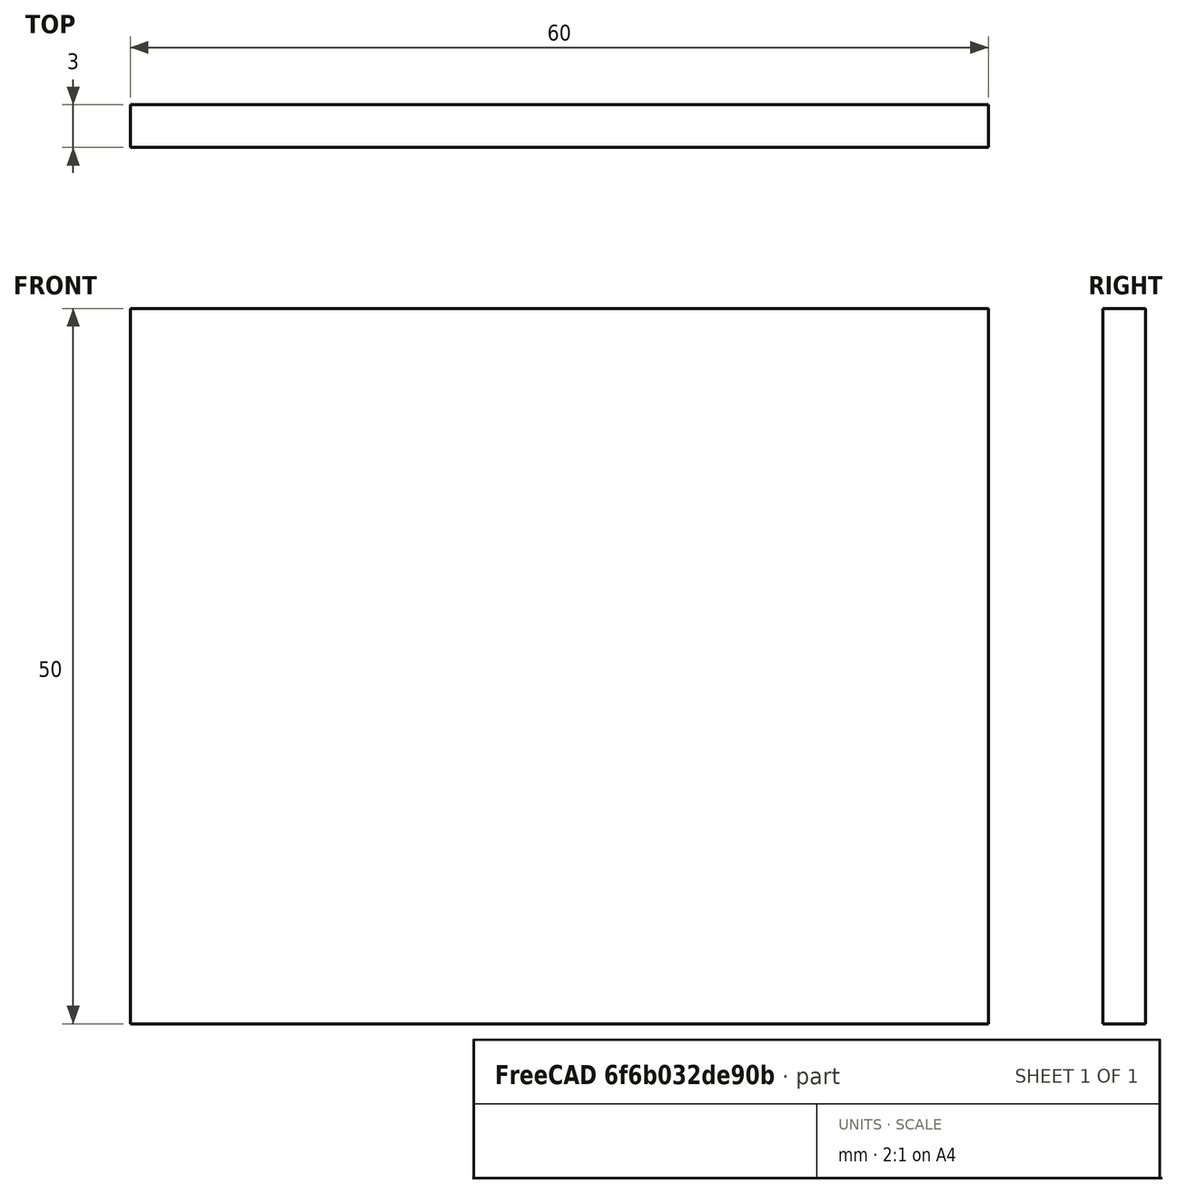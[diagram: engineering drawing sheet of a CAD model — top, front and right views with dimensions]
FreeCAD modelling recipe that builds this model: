
FCSTD DOCUMENT  (FreeCAD 0.15R4671 (Git))
Label: Flat Bar 60x3 EN10058 S235JR
License: All rights reserved
LicenseURL: http://en.wikipedia.org/wiki/All_rights_reserved
objects: Sketcher::SketchObject×1, Part::Extrusion×1
note: 2 computed .brp shape members not serialized (recipe doc carries the construction recipe); baked Part::Feature solids carry a one-line shape summary decoded from their .brp

FEATURE [Sketcher::SketchObject] Sketch
  sketch-geometry (4):
    g0: LineSegment StartX=-30 StartY=-1.5 StartZ=0 EndX=30 EndY=-1.5 EndZ=0
    g1: LineSegment StartX=30 StartY=-1.5 StartZ=0 EndX=30 EndY=1.5 EndZ=0
    g2: LineSegment StartX=30 StartY=1.5 StartZ=0 EndX=-30 EndY=1.5 EndZ=0
    g3: LineSegment StartX=-30 StartY=1.5 StartZ=0 EndX=-30 EndY=-1.5 EndZ=0
  constraints (12):
    c: Coincident(g0,g1)
    c: Coincident(g1,g2)
    c: Coincident(g2,g3)
    c: Coincident(g3,g0)
    c: Horizontal(g0)
    c: Horizontal(g2)
    c: Vertical(g1)
    c: Vertical(g3)
    c: Symmetric(g1,g2,g-2)
    c: Symmetric(g0,g1,g-1)
    c: DistanceY(g1) = 3
    c: DistanceX(g0) = 60
FEATURE [Part::Extrusion] Extrude  label="Flat Bar 60x3 EN10058 S235JR"
  Base = -> Sketch
  Dir = (0,0,50)
  Solid = true
